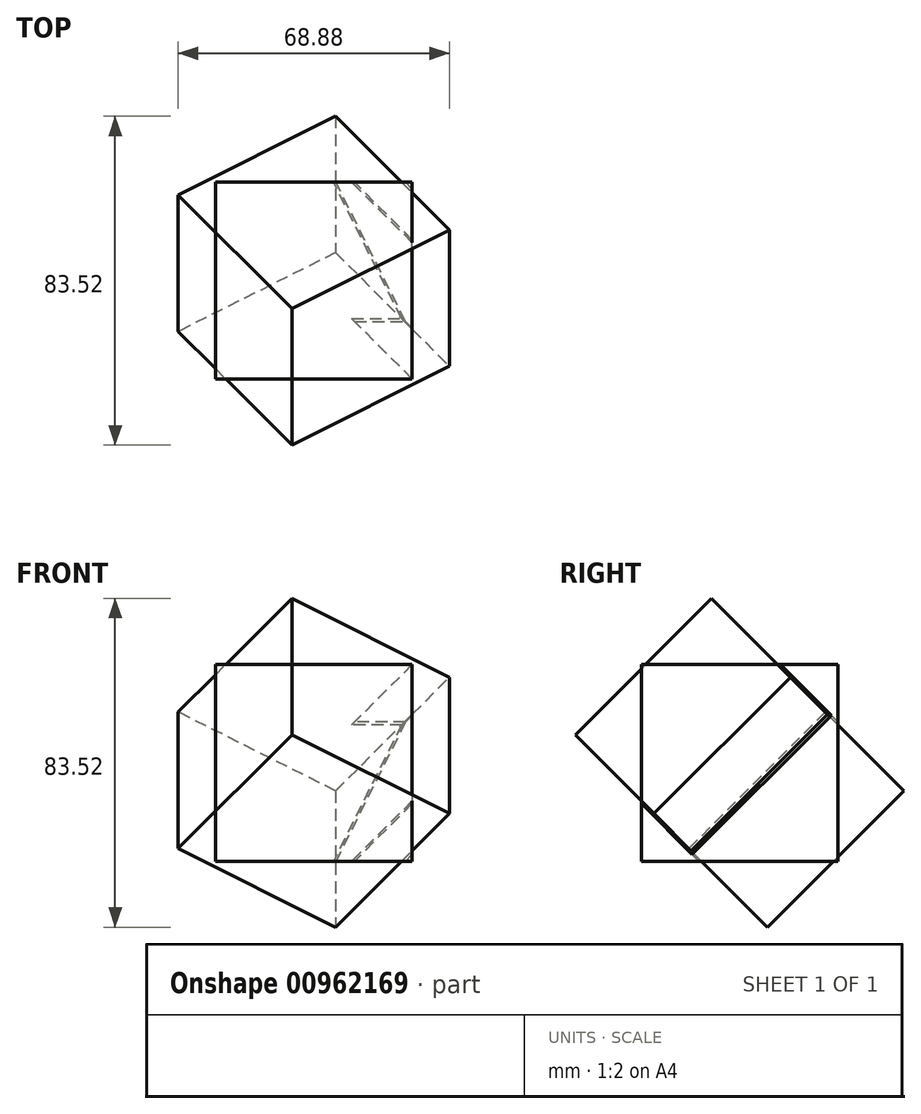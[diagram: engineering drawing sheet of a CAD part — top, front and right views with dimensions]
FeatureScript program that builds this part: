
annotation { "Feature Type Name" : "Feature", "Feature Type Description" : "" }
export const myFeature = defineFeature(function(context is Context, id is Id, definition is map)
    precondition{}
    {
        {
            assignVariable(context, id + "F0", {"name" : "side", "anyValue" : 50});
        }
        {
            var Q0;
            Q0=qCreatedBy(makeId("Top.planeOp"),FACE);
            var sketch = newSketch(context, id + "F1", { "sketchPlane" : qUnion([Q0])});
            skLineSegment(sketch, "E0.bottom", {"start": v(-25, -25) * mm, "end": v(25, -25) * mm});
            skLineSegment(sketch, "E0.top", {"start": v(-25, 25) * mm, "end": v(25, 25) * mm});
            skLineSegment(sketch, "E0.left", {"start": v(-25, -25) * mm, "end": v(-25, 25) * mm});
            skLineSegment(sketch, "E0.right", {"start": v(25, -25) * mm, "end": v(25, 25) * mm});
            skPoint(sketch, "E0.middle", {"position": v(0, 0) * mm});
            skSolve(sketch);
        }
        {
            var Q0;
            Q0=makeQuery(id+"F1.imprint","IMPRINT",FACE,{"disambiguationData":[TD([[makeQuery(id+"F1.imprint","IMPRINT",EDGE,{"derivedFrom":sQuery(id+"F1.wireOp",EDGE,"E0.bottom")}),1.0]])]});
            extrude(context, id + "F2", {"entities" : qUnion([Q0]), "endBound" : BoundingType.SYMMETRIC, "depth" : (getVariable(context, 'side')) * mm, "offsetDistance" : 25 * mm});
        }
        {
            var Q0;
            Q0=makeQuery(id+"F2.opExtrude","CAP_VERTEX",VERTEX,{"disambiguationData":[OSD([sQuery(id+"F1.wireOp",EDGE,"E0.bottom"),sQuery(id+"F1.wireOp",EDGE,"E0.right")])],"isStart":false});
            var Q1;
            Q1=makeQuery(id+"F2.opExtrude","CAP_VERTEX",VERTEX,{"disambiguationData":[OSD([sQuery(id+"F1.wireOp",EDGE,"E0.top"),sQuery(id+"F1.wireOp",EDGE,"E0.left")])],"isStart":true});
            cPlane(context, id + "F3", {"entities" : qUnion([Q0, Q1]), "cplaneType" : CPlaneType.MID_PLANE, "offset" : 25 * mm, "width" : 150 * mm, "height" : 150 * mm});
        }
        {
            var Q0;
            Q0=qCreatedBy(id+"F3.planeOp",FACE);
            var sketch = newSketch(context, id + "F4", { "sketchPlane" : qUnion([Q0])});
            skLineSegment(sketch, "E1", {"start": v(30.62, 17.68) * mm, "end": v(0, 35.36) * mm, "construction": true});
            skLineSegment(sketch, "E2", {"start": v(30.62, -17.68) * mm, "end": v(0, -35.36) * mm, "construction": true});
            skLineSegment(sketch, "E3", {"start": v(-30.62, -17.68) * mm, "end": v(-30.62, 17.68) * mm, "construction": true});
            skLineSegment(sketch, "E4", {"start": v(30.62, -17.68) * mm, "end": v(30.62, 17.68) * mm, "construction": true});
            skLineSegment(sketch, "E5", {"start": v(0, -35.36) * mm, "end": v(-30.62, -17.68) * mm, "construction": true});
            skLineSegment(sketch, "E6", {"start": v(0, 35.36) * mm, "end": v(-30.62, 17.68) * mm, "construction": true});
            skLineSegment(sketch, "E7.0.0", {"start": v(-20.41, -35.36) * mm, "end": v(-40.82, 0) * mm});
            skLineSegment(sketch, "E7.0.1", {"start": v(-40.82, 0) * mm, "end": v(-20.41, 35.36) * mm});
            skLineSegment(sketch, "E7.0.2", {"start": v(-20.41, 35.36) * mm, "end": v(0, 0) * mm});
            skLineSegment(sketch, "E7.0.3", {"start": v(0, 0) * mm, "end": v(-20.41, -35.36) * mm});
            skLineSegment(sketch, "E8.0.0", {"start": v(-20.41, 35.36) * mm, "end": v(20.41, 35.36) * mm});
            skLineSegment(sketch, "E8.0.1", {"start": v(20.41, 35.36) * mm, "end": v(40.82, 0) * mm});
            skLineSegment(sketch, "E8.0.2", {"start": v(40.82, 0) * mm, "end": v(0, 0) * mm});
            skLineSegment(sketch, "E8.0.3", {"start": v(0, 0) * mm, "end": v(-20.41, 35.36) * mm});
            skLineSegment(sketch, "E9.0.0", {"start": v(20.41, -35.36) * mm, "end": v(-20.41, -35.36) * mm});
            skLineSegment(sketch, "E9.0.1", {"start": v(-20.41, -35.36) * mm, "end": v(0, 0) * mm});
            skLineSegment(sketch, "E9.0.2", {"start": v(0, 0) * mm, "end": v(40.82, 0) * mm});
            skLineSegment(sketch, "E9.0.3", {"start": v(40.82, 0) * mm, "end": v(20.41, -35.36) * mm});
            skLineSegment(sketch, "E10.bottom", {"start": v(-25, 25) * mm, "end": v(25, 25) * mm});
            skLineSegment(sketch, "E10.top", {"start": v(-25, -25) * mm, "end": v(25, -25) * mm});
            skLineSegment(sketch, "E10.left", {"start": v(-25, 25) * mm, "end": v(-25, -25) * mm});
            skLineSegment(sketch, "E10.right", {"start": v(25, 25) * mm, "end": v(25, -25) * mm});
            skPoint(sketch, "E10.middle", {"position": v(0, 0) * mm});
            skLineSegment(sketch, "E11.0", {"start": v(-24.5, 24.5) * mm, "end": v(24.5, 24.5) * mm});
            skLineSegment(sketch, "E11.1", {"start": v(-24.5, 24.5) * mm, "end": v(-24.5, -24.5) * mm});
            skLineSegment(sketch, "E11.2", {"start": v(-24.5, -24.5) * mm, "end": v(24.5, -24.5) * mm});
            skLineSegment(sketch, "E11.3", {"start": v(24.5, 24.5) * mm, "end": v(24.5, -24.5) * mm});
            skSolve(sketch);
        }
        {
            var Q0;
            {var subQ3=sQuery(id+"F4.wireOp",EDGE,"E8.0.3");var subQ5=sQuery(id+"F4.wireOp",EDGE,"E11.0");var subQ6=makeQuery(id+"F4.imprint","INTERSECT",VERTEX,{"derivedFrom":[subQ3,subQ5]});Q0=makeQuery(id+"F4.imprint","IMPRINT",FACE,{"disambiguationData":[TD([[makeQuery(id+"F4.imprint","IMPRINT",EDGE,{"disambiguationData":[TD([[subQ6,-1.0]])],"derivedFrom":subQ3}),-1.0]])]});}
            var Q1;
            {var subQ0=sQuery(id+"F4.wireOp",EDGE,"E10.left");Q1=makeQuery(id+"F4.imprint","IMPRINT",FACE,{"disambiguationData":[TD([[makeQuery(id+"F4.imprint","IMPRINT",EDGE,{"derivedFrom":subQ0}),1.0]])]});}
            var Q2;
            {var subQ1=sQuery(id+"F4.wireOp",EDGE,"E10.top");var subQ5=sQuery(id+"F4.wireOp",EDGE,"E9.0.1");var subQ6=makeQuery(id+"F4.imprint","INTERSECT",VERTEX,{"derivedFrom":[subQ5,subQ1]});Q2=makeQuery(id+"F4.imprint","IMPRINT",FACE,{"disambiguationData":[TD([[makeQuery(id+"F4.imprint","IMPRINT",EDGE,{"disambiguationData":[TD([[subQ6,-1.0]])],"derivedFrom":subQ5}),-1.0]])]});}
            extrude(context, id + "F5", {"entities" : qUnion([Q0, Q1, Q2]), "operationType" : NewBodyOperationType.REMOVE, "endBound" : BoundingType.THROUGH_ALL, "oppositeDirection" : true, "depth" : 212.8 * mm, "offsetDistance" : 25 * mm, "hasSecondDirection" : true, "secondDirectionBound" : SecondDirectionBoundingType.THROUGH_ALL, "secondDirectionOppositeDirection" : false, "secondDirectionDepth" : 25 * mm});
        }
        {
            var Q0;
            {var subQ3=sQuery(id+"F4.wireOp",EDGE,"E11.0");var subQ5=sQuery(id+"F4.wireOp",EDGE,"E11.3");var subQ7=makeQuery(id+"F4.imprint","INTERSECT",VERTEX,{"derivedFrom":[subQ3,subQ5]});Q0=makeQuery(id+"F4.imprint","IMPRINT",FACE,{"disambiguationData":[TD([[makeQuery(id+"F4.imprint","IMPRINT",EDGE,{"disambiguationData":[TD([[subQ7,1.0]])],"derivedFrom":subQ3}),-1.0]])]});}
            var Q1;
            {var subQ3=sQuery(id+"F4.wireOp",EDGE,"E11.2");var subQ5=sQuery(id+"F4.wireOp",EDGE,"E11.3");var subQ7=makeQuery(id+"F4.imprint","INTERSECT",VERTEX,{"derivedFrom":[subQ3,subQ5]});Q1=makeQuery(id+"F4.imprint","IMPRINT",FACE,{"disambiguationData":[TD([[makeQuery(id+"F4.imprint","IMPRINT",EDGE,{"disambiguationData":[TD([[subQ7,1.0]])],"derivedFrom":subQ3}),1.0]])]});}
            var Q2;
            {var subQ0=sQuery(id+"F4.wireOp",EDGE,"E11.1");Q2=makeQuery(id+"F4.imprint","IMPRINT",FACE,{"disambiguationData":[TD([[makeQuery(id+"F4.imprint","IMPRINT",EDGE,{"derivedFrom":subQ0}),1.0]])]});}
            extrude(context, id + "F6", {"entities" : qUnion([Q0, Q1, Q2]), "endBound" : BoundingType.SYMMETRIC, "depth" : (getVariable(context, 'side')) * mm, "offsetDistance" : 25 * mm});
        }
    });
